# Revit family: 01 ISKU Rudolf
name_source: partatom
category: Furniture
revit_build: Autodesk Revit 2015 (Build: 20140606_1530(x64)
units: mm (PartAtom-declared; Revit-internal decimal feet)

## types (8) — shared parameters
Available as antimicrobial = Yes
Manufacturer = Isku Oy
URL = www.isku.fi
zero-valued in all types: NominalDepth, NominalHeight, NominalLength

## per-type parameters (varying)
| type | Depth | Height | Model | Rudolf type | Width |
| 01 Rudolf bar stool, high back, wooden legs | 471 mm  [stored 1.54528 ft] | 1030 mm  [stored 3.37927 ft] | 3209 | 01 Rudolf bar stool, high back, wooden legs | 455 mm |
| 02 Rudolf bar stool, low back, wooden legs | 471 mm  [stored 1.54528 ft] | 820 mm  [stored 2.69029 ft] | 3209 | 02 Rudolf bar stool, low back, wooden legs | 455 mm |
| 03 Rudolf chair, high back, wooden legs | 510 mm  [stored 1.67323 ft] | 910 mm | 3209 | 03 Rudolf chair, high back, wooden legs | 430 mm |
| 04 Rudolf chair, low back, wooden legs | 510 mm  [stored 1.67323 ft] | 830 mm  [stored 2.7231 ft] | 3209 | 04 Rudolf chair, low back, wooden legs | 430 mm |
| 05 Rudolf bar stool, loop leg 650, high back, not stackable | 471 mm  [stored 1.54528 ft] | 1030 mm  [stored 3.37927 ft] | 3211 | 05 Rudolf bar stool, high back, wooden legs | 455 mm |
| 06 Rudolf bar stool, loop leg 650, low back, not stackable lower leg | 471 mm  [stored 1.54528 ft] | 825 mm  [stored 2.70669 ft] | 3211 | 06 Rudolf bar stool, loop leg 650, low back, not stackable lower leg | 455 mm |
| 07 Rudolf bar stool, loop leg, low back, not stackable | 483 mm | 731 mm  [stored 2.39829 ft] | 3211 | 07 Rudolf bar stool, loop leg, low back, not stackable | 500 mm  [stored 1.64042 ft] |
| 08 Rudolf bar stool, not stackable, high back, loop leg | 483 mm | 936 mm  [stored 3.07087 ft] | 3211 | 08 Rudolf bar stool, loop leg, low back, not stackable | 500 mm  [stored 1.64042 ft] |

note: [stored X ft] marks values corroborated as IEEE doubles in the binary element streams (Revit-internal decimal feet)

## geometry (parser evidence)
native form markers: Sweep x96
no freeform markers — native parametric forms only
